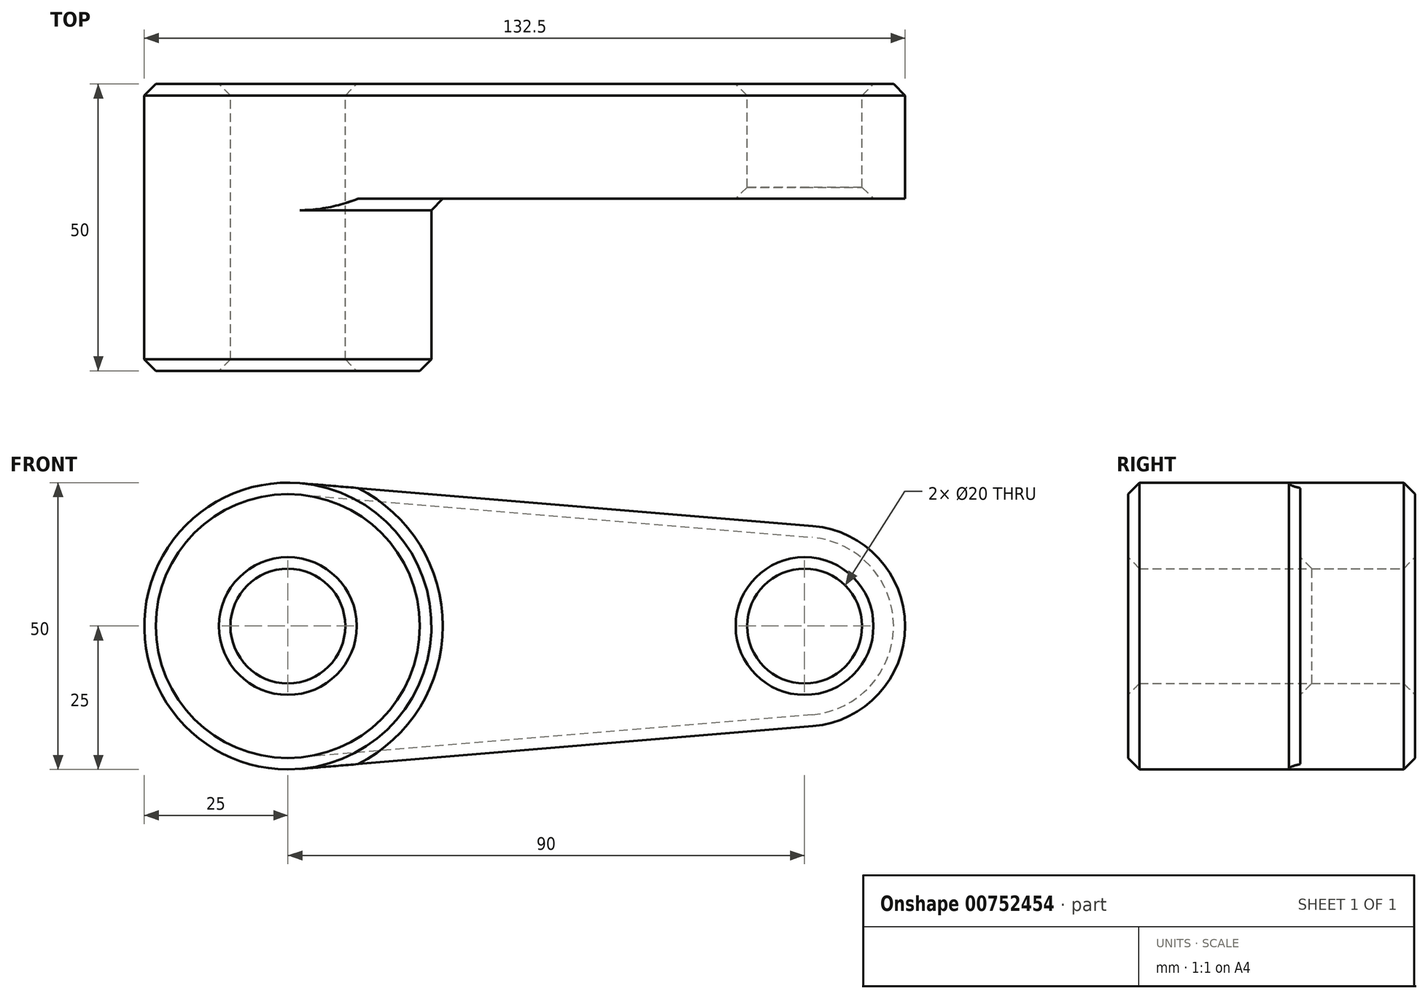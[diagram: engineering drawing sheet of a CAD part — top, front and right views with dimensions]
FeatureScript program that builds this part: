
annotation { "Feature Type Name" : "Feature", "Feature Type Description" : "" }
export const myFeature = defineFeature(function(context is Context, id is Id, definition is map)
    precondition{}
    {
        {
            var Q0;
            Q0=qCreatedBy(makeId("Front.planeOp"),FACE);
            var sketch = newSketch(context, id + "F0", { "sketchPlane" : qUnion([Q0])});
            skCircle(sketch, "E0", {"center": v(0, 0) * mm, "radius": 25 * mm});
            skCircle(sketch, "E1", {"center": v(90, 0) * mm, "radius": 17.5 * mm});
            skLineSegment(sketch, "E2", {"start": v(2.08, 24.91) * mm, "end": v(91.46, 17.44) * mm});
            skLineSegment(sketch, "E3", {"start": v(2.08, -24.91) * mm, "end": v(91.46, -17.44) * mm});
            skCircle(sketch, "E4", {"center": v(0, 0) * mm, "radius": 10 * mm});
            skCircle(sketch, "E5", {"center": v(90, 0) * mm, "radius": 10 * mm});
            skSolve(sketch);
        }
        {
            var Q0;
            Q0 = qSketchRegion(id + "F0", true);
            extrude(context, id + "F1", {"entities" : qUnion([Q0]), "depth" : 20 * mm, "offsetDistance" : 25 * mm});
        }
        {
            var Q0;
            Q0=makeQuery(id+"F0.imprint","IMPRINT",FACE,{"disambiguationData":[TD([[makeQuery(id+"F0.imprint","IMPRINT",EDGE,{"derivedFrom":sQuery(id+"F0.wireOp",EDGE,"E4")}),-1.0]])]});
            extrude(context, id + "F2", {"entities" : qUnion([Q0]), "operationType" : NewBodyOperationType.ADD, "depth" : 50 * mm, "offsetDistance" : 25 * mm});
        }
        {
            var Q0;
            {var subQ0=sQuery(id+"F0.wireOp",EDGE,"E4");Q0=makeQuery(id+"F2.boolean.opBoolean","MERGE",FACE,{"derivedFrom":[makeQuery(id+"F1.opExtrude","SWEPT_FACE",FACE,{"disambiguationData":[OSD([subQ0])]}),makeQuery(id+"F2.opExtrude","SWEPT_FACE",FACE,{"disambiguationData":[OSD([subQ0])]})]});}
            var Q1;
            {var subQ0=sQuery(id+"F0.wireOp",EDGE,"E0");Q1=makeQuery(id+"F2.boolean.opBoolean","MERGE",FACE,{"derivedFrom":[makeQuery(id+"F1.opExtrude","SWEPT_FACE",FACE,{"disambiguationData":[OSD([subQ0])]}),makeQuery(id+"F2.opExtrude","SWEPT_FACE",FACE,{"disambiguationData":[OSD([subQ0])]})]});}
            var Q2;
            Q2=makeQuery(id+"F1.opExtrude","SWEPT_FACE",FACE,{"disambiguationData":[OSD([sQuery(id+"F0.wireOp",EDGE,"E5")])]});
            chamfer(context, id + "F3", {"entities" : qUnion([Q0, Q1, Q2]), "width" : 2 * mm, "tangentPropagation" : true});
        }
    });
